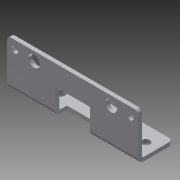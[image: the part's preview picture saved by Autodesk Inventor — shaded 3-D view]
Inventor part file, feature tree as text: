
AUTODESK INVENTOR PART (.ipt)
format: ipt  version: 2013 (Build 170138000, 138)  size: 262,656 bytes
history: native  units: in
note: dims shown in document units (in); Inventor stores cm internally (conversion verified against a paired STEP export)
features: other x7, sketch x6, sheet_metal_op x4, reference x3, chamfer x1, plane x1
ambient origin geometry x8: Origin, YZ Plane, XZ Plane, XY Plane, X Axis, Y Axis, Z Axis, Center Point
bodies: Solid1 (feature_tree)
feature tree (22):
  sheet_metal_op  "Face1"
  sheet_metal_op  "Flange1"
  chamfer  "Corner Round1"
  plane  "Work Plane1"
  sketch  "Sketch1"  dims[d0=4.25in]
  other  "Plate1"
  sketch  "Sketch2"  dims[d1=1.125in]
  other  "Plate2"
  sheet_metal_op  "Bend1"
  sheet_metal_op  "Corner1"
  sketch  "Sketch3"  dims[d3=0.125in]
  sketch  "Sketch4"  dims[d4=0.125in]
  sketch  "Sketch5"  dims[d5=0.0625in]
  reference  "Reference1"
  sketch  "Sketch6"  dims[d6=0.25in d7=0.125in d8=1.5in d9=90.0deg d10=0.05in d11=0.5in d12=0.125in d13=0.125in d18=1.125in d20=0.375in d21=0.0in d22=0.625in d23=0.26in d24=0.26in d25=2.0in d26=1.0in d27=0.125in d28=0.0in d29=0.125in d30=0.125in d31=0.0in d32=0.125in d33=0.0in d34=0.375in d35=0.375in d36=0.875in d37=0.875in d38=0.25in d39=0.25in d2=0.125in]
  reference  "Reference11"
  reference  "Reference12"
  other  "Cut1"
  other  "Cut2"
  other  "Cut3"
  other  "Cut4"
  other  "Definition1"
